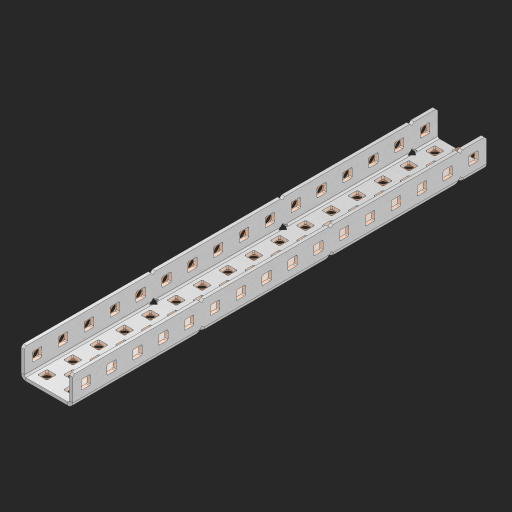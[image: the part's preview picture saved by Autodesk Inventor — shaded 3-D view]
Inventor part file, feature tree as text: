
AUTODESK INVENTOR PART (.ipt)
format: ipt  version: 2023 (Build 270158000, 158)  size: 1,216,512 bytes
history: native  units: in
note: dims shown in document units (in); Inventor stores cm internally (conversion verified against a paired STEP export)
features: other x87, extrude x78, sheet_metal_op x11, sketch x10, pattern_linear x2, mirror x1, chamfer x1
ambient origin geometry x8: Origin, YZ Plane, XZ Plane, XY Plane, X Axis, Y Axis, Z Axis, Center Point
bodies: Solid1 (feature_tree), Body (feature_tree)
feature tree (190):
  sheet_metal_op  "Flanges"
  other  "Flange Pattern Plane"
  other  "Flange Pattern Sketch"
  sheet_metal_op  "Flange Pattern"
  sheet_metal_op  "Body Pattern"
  pattern_linear  "Center Pattern"  Spacing1=0.0625in  [1 undecoded]
  other  "Arc Length"
  mirror  "Notch Mirror"
  pattern_linear  "Notch Pattern"  Spacing1=0.182in  [1 undecoded]
  chamfer  "End Chamfer"
  extrude  "Half Cut"  Depth=0.02in
  sketch  "Sketch1"  dims[d0=1.0in]
  other  "Plate1"
  sketch  "Sketch2"  dims[d1=8.0in]
  other  "Plate2"
  sheet_metal_op  "Bend1"
  sheet_metal_op  "Corner1"
  sketch  "Sketch3"  dims[d2=0.0625in]
  sketch  "Sketch7"  dims[d3=0.0625in]
  other  "Srf1"
  other  "Srf2"
  sketch  "Sketch8"  dims[d4=0.0312in]
  sketch  "Sketch9"  dims[d5=0.125in]
  other  "Srf91"
  sheet_metal_op  "Body Pattern Sketch"
  other  "Srf92"
  sketch  "Sketch13"  dims[d6=0.0625in]
  sketch  "Sketch14"  dims[d7=0.5in d8=90.0deg d9=0.0312in]
  sketch  "Sketch15"  dims[d10=0.25in]
  sketch  "Sketch16"  dims[d11=0.0625in d12=0.0625in d16=0.182in d17=0.02in d18=0.0625in d19=0.0in d20=0.25in d21=0.25in d38=6.2992in d40=0.5in d41=0.7874in d43=1.0in d46=0.172in d47=1.0in d48=0.0in d49=0.182in d50=0.02in d51=0.25in d52=0.25in d53=0.0625in d54=0.0in d55=0.172in d56=1.0in d57=0.0in d58=0.25in d60=6.2992in d62=0.5in d63=0.7874in d65=0.5in d85=0.1473in d86=0.1782in d88=0.04in d89=0.0625in d90=0.0in d91=0.04in d92=0.0491in d95=2.5in d96=0.04in d97=0.25in d98=45.0deg d99=0.25in d100=0.5in d101=0.0in d102=2.497in d106=0.182in d107=0.02in d108=0.5in d109=0.5in d110=0.0625in d111=0.0in d112=0.172in d113=0.5in d114=0.0in d117=0.5in d118=0.5in d119=0.5in]
  other  "Srf786"
  other  "Srf823"
  other  "Srf824"
  other  "Srf825"
  other  "Srf826"
  other  "Srf827"
  other  "Srf828"
  other  "Srf829"
  other  "Srf856"
  other  "Srf857"
  other  "Srf858"
  other  "Srf859"
  other  "Srf860"
  other  "Srf861"
  other  "Srf862"
  other  "Srf889"
  other  "Srf890"
  other  "Srf891"
  other  "Srf892"
  other  "Srf893"
  other  "Srf894"
  other  "Srf895"
  other  "Srf896"
  other  "Srf922"
  other  "Srf923"
  other  "Srf924"
  other  "Srf925"
  other  "Srf926"
  other  "Srf959"
  other  "Srf960"
  other  "Srf961"
  other  "Srf962"
  other  "Srf963"
  other  "Srf996"
  other  "Srf997"
  other  "Srf998"
  other  "Srf999"
  other  "Srf1000"
  other  "Srf1143"
  other  "Srf1144"
  other  "Srf1145"
  other  "Srf1146"
  other  "Srf1147"
  other  "Srf1148"
  other  "Srf1149"
  other  "Srf1150"
  other  "Srf1151"
  other  "Srf1152"
  other  "Srf1153"
  other  "Srf1154"
  other  "Srf1155"
  other  "Srf1156"
  other  "Srf1157"
  other  "Srf1158"
  other  "Srf1159"
  other  "Srf1160"
  other  "Srf1199"
  other  "Srf1200"
  other  "Srf1201"
  other  "Srf1202"
  other  "Srf1203"
  other  "Srf1204"
  other  "Srf1205"
  other  "Srf1206"
  other  "Srf1207"
  other  "Srf1208"
  other  "Srf1209"
  other  "Srf1210"
  other  "Srf1211"
  other  "Srf1212"
  other  "Srf1213"
  other  "Srf1214"
  other  "Srf1215"
  other  "Srf1216"
  other  "Srf1255"
  other  "Srf1256"
  sheet_metal_op  "Flange Stamp"
  sheet_metal_op  "Flange Circle"
  sheet_metal_op  "Body Stamp"
  sheet_metal_op  "Body Circle"
  other  "Center Stamp"
  other  "Center Circle"
  sheet_metal_op  "Notch"
  extrude  "ExtrusionSrf2"  Depth=0.0625in
  extrude  "ExtrusionSrf92"  TaperAngle=0.0deg  [1 undecoded]
  extrude  "ExtrusionSrf823"  Depth=0.5in
  extrude  "ExtrusionSrf824"  Depth=0.5in
  extrude  "ExtrusionSrf825"  Depth=0.5in
  extrude  "ExtrusionSrf826"  Depth=0.5in
  extrude  "ExtrusionSrf827"  Depth=1.0in TaperAngle=0.0deg
  extrude  "ExtrusionSrf828"  Depth=0.5in
  extrude  "ExtrusionSrf829"  Depth=0.02in
  extrude  "ExtrusionSrf856"  Depth=0.5in
  extrude  "ExtrusionSrf857"  Depth=0.5in
  extrude  "ExtrusionSrf858"  Depth=0.0625in
  extrude  "ExtrusionSrf859"  TaperAngle=0.0deg  [1 undecoded]
  extrude  "ExtrusionSrf860"  Depth=0.5in
  extrude  "ExtrusionSrf861"  Depth=1.0in TaperAngle=0.0deg
  extrude  "ExtrusionSrf862"  Depth=0.5in
  extrude  "ExtrusionSrf889"  Depth=0.5in
  extrude  "ExtrusionSrf890"  Depth=0.5in
  extrude  "ExtrusionSrf891"  Depth=0.5in
  extrude  "ExtrusionSrf892"  Depth=0.5in
  extrude  "ExtrusionSrf893"  Depth=0.5in
  extrude  "ExtrusionSrf894"  Depth=0.0625in
  extrude  "ExtrusionSrf895"  TaperAngle=0.0deg  [1 undecoded]
  extrude  "ExtrusionSrf896"  Depth=0.5in
  extrude  "ExtrusionSrf922"  Depth=0.5in
  extrude  "ExtrusionSrf923"  Depth=2.5in
  extrude  "ExtrusionSrf924"  Depth=0.5in TaperAngle=45.0deg
  extrude  "ExtrusionSrf925"  Depth=0.5in
  extrude  "ExtrusionSrf926"  Depth=0.5in TaperAngle=0.0deg
  extrude  "ExtrusionSrf959"  Depth=0.5in
  extrude  "ExtrusionSrf960"  Depth=0.5in
  extrude  "ExtrusionSrf961"  Depth=0.02in
  extrude  "ExtrusionSrf962"  Depth=0.5in
  extrude  "ExtrusionSrf963"  Depth=0.5in
  extrude  "ExtrusionSrf996"  Depth=0.0625in
  extrude  "ExtrusionSrf997"  TaperAngle=0.0deg  [1 undecoded]
  extrude  "ExtrusionSrf998"  Depth=0.5in
  extrude  "ExtrusionSrf999"  Depth=0.5in TaperAngle=0.0deg
  extrude  "ExtrusionSrf1000"  Depth=0.5in
  extrude  "ExtrusionSrf1143"  Depth=0.5in
  extrude  "ExtrusionSrf1144"  Depth=0.5in
  extrude  "ExtrusionSrf1145"  [1 undecoded]
  extrude  "ExtrusionSrf1146"  [1 undecoded]
  extrude  "ExtrusionSrf1147"  [1 undecoded]
  extrude  "ExtrusionSrf1148"  [1 undecoded]
  extrude  "ExtrusionSrf1149"  [1 undecoded]
  extrude  "ExtrusionSrf1150"  [1 undecoded]
  extrude  "ExtrusionSrf1151"  [1 undecoded]
  extrude  "ExtrusionSrf1152"  [1 undecoded]
  extrude  "ExtrusionSrf1153"  [1 undecoded]
  extrude  "ExtrusionSrf1154"  [1 undecoded]
  extrude  "ExtrusionSrf1155"  [1 undecoded]
  extrude  "ExtrusionSrf1156"  [1 undecoded]
  extrude  "ExtrusionSrf1157"  [1 undecoded]
  extrude  "ExtrusionSrf1158"  [1 undecoded]
  extrude  "ExtrusionSrf1159"  [1 undecoded]
  extrude  "ExtrusionSrf1160"  [1 undecoded]
  extrude  "ExtrusionSrf1199"  [1 undecoded]
  extrude  "ExtrusionSrf1200"  [1 undecoded]
  extrude  "ExtrusionSrf1201"  [1 undecoded]
  extrude  "ExtrusionSrf1202"  [1 undecoded]
  extrude  "ExtrusionSrf1203"  [1 undecoded]
  extrude  "ExtrusionSrf1204"  [1 undecoded]
  extrude  "ExtrusionSrf1205"  [1 undecoded]
  extrude  "ExtrusionSrf1206"  [1 undecoded]
  extrude  "ExtrusionSrf1207"  [1 undecoded]
  extrude  "ExtrusionSrf1208"  [1 undecoded]
  extrude  "ExtrusionSrf1209"  [1 undecoded]
  extrude  "ExtrusionSrf1210"  [1 undecoded]
  extrude  "ExtrusionSrf1211"  [1 undecoded]
  extrude  "ExtrusionSrf1212"  [1 undecoded]
  extrude  "ExtrusionSrf1213"  [1 undecoded]
  extrude  "ExtrusionSrf1214"  [1 undecoded]
  extrude  "ExtrusionSrf1215"  [1 undecoded]
  extrude  "ExtrusionSrf1216"  [1 undecoded]
  extrude  "ExtrusionSrf1255"  [1 undecoded]
  extrude  "ExtrusionSrf1256"  [1 undecoded]
note: 42 required parameter values undecoded (feature->parameter linkage not recoverable at this tier; creation-order binding heuristic only, values carry confidence <= 0.55)
